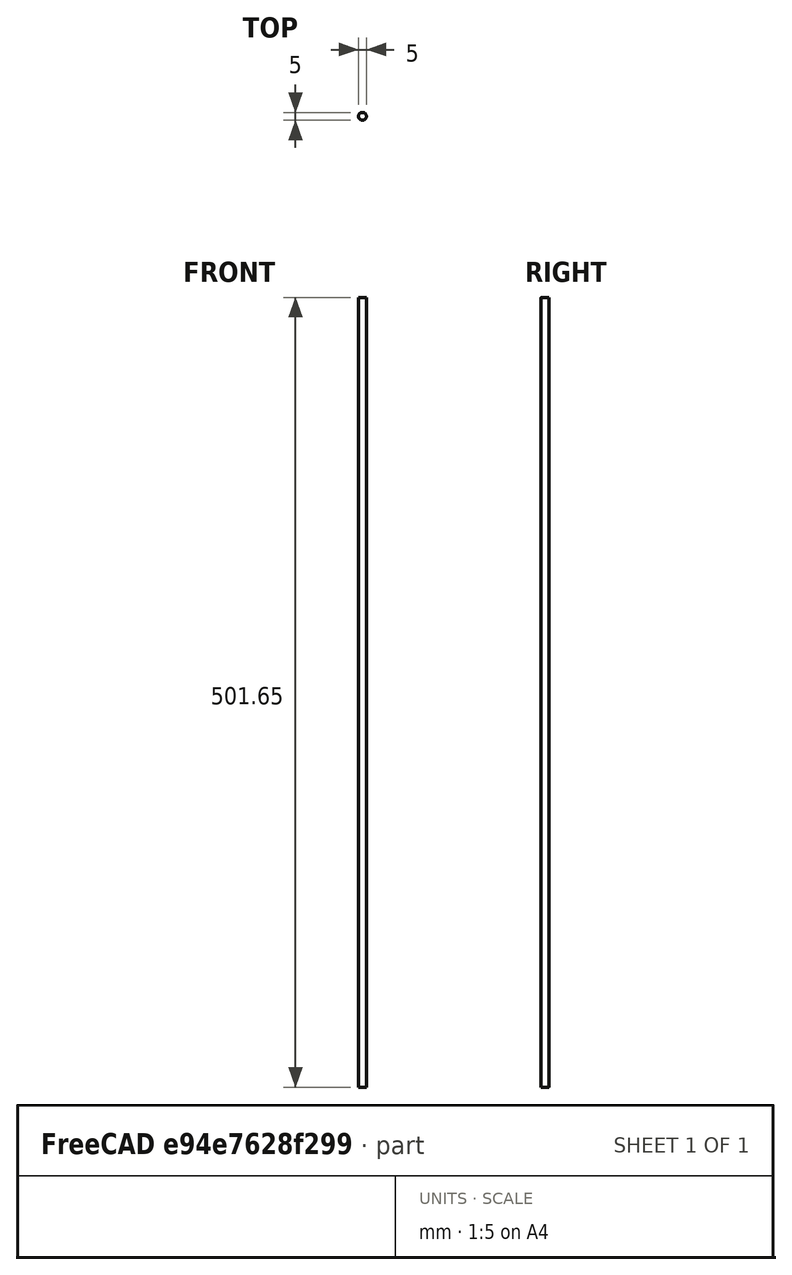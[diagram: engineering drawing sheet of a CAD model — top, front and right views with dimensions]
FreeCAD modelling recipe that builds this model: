
FCSTD DOCUMENT  (FreeCAD 0.20R29603 (Git))
Label: cross rod
License: All rights reserved
LicenseURL: http://en.wikipedia.org/wiki/All_rights_reserved
objects: Sketcher::SketchObject×1, PartDesign::Pad×1, PartDesign::Body×1, Spreadsheet::Sheet×1, App::Part×1
note: 4 computed .brp shape members not serialized (recipe doc carries the construction recipe); baked Part::Feature solids carry a one-line shape summary decoded from their .brp

FEATURE [Sketcher::SketchObject] Sketch
  FullyConstrained = true
  MapMode = 5
  Support = -> [XY_Plane]
  expr: Constraints[1] = <<cross_rod_dims>>.cross_rod_diameter
  sketch-geometry (1):
    g0: Circle CenterX=0 CenterY=0 CenterZ=0 NormalX=0 NormalY=0 NormalZ=1 AngleXU=0 Radius=2.5
  constraints (2):
    c: Coincident(g0,g-1)
    c: Diameter(g0) = 5
FEATURE [PartDesign::Pad] Pad
  Direction = (0,0,1)
  Length = 501.65
  Length2 = 10
  Profile = -> Sketch
  ReferenceAxis = -> Sketch [N_Axis]
  Type = 0
  expr: Length = <<cross_rod_dims>>.cross_rod_length
FEATURE [PartDesign::Body] Body  label="cross rod"
  Group = -> [Sketch,Pad]
  Origin = -> Origin
  Tip = -> Pad
FEATURE [Spreadsheet::Sheet] Spreadsheet  label="cross_rod_dims"
  cells = A1=cross_rod_diameter; B1(cross_rod_diameter)=5; A2=cross_rod_length; B2(cross_rod_length)=501.65
FEATURE [App::Part] Part  label="cross rod part"
  Group = -> [Body,Spreadsheet]
  Origin = -> Origin001
